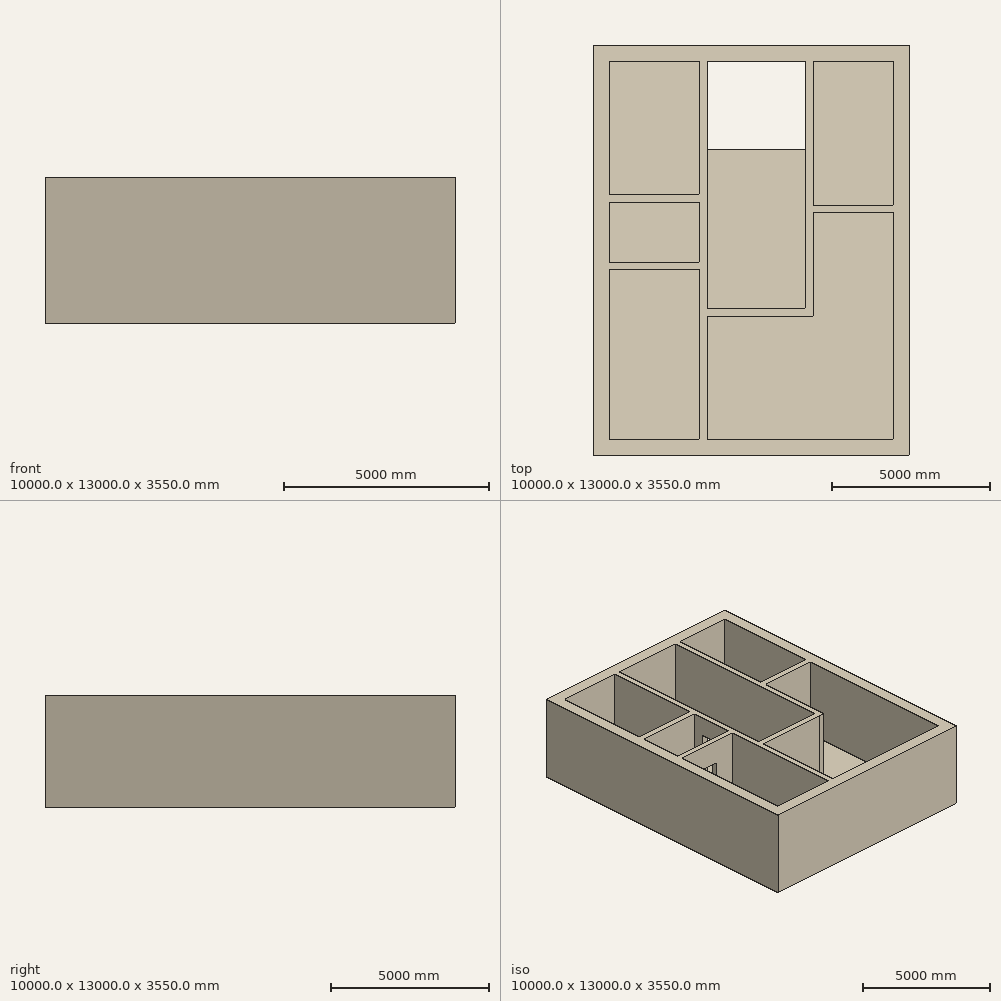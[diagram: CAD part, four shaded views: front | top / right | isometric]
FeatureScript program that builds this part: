
annotation { "Feature Type Name" : "Feature", "Feature Type Description" : "" }
export const myFeature = defineFeature(function(context is Context, id is Id, definition is map)
    precondition{}
    {
        {
            var Q0;
            Q0=qCreatedBy(makeId("Top.planeOp"),FACE);
            var sketch = newSketch(context, id + "F0", { "sketchPlane" : qUnion([Q0])});
            skLineSegment(sketch, "E0.bottom", {"start": v(5000, 6500) * mm, "end": v(-5000, 6500) * mm});
            skLineSegment(sketch, "E0.top", {"start": v(5000, -6500) * mm, "end": v(-5000, -6500) * mm});
            skLineSegment(sketch, "E0.left", {"start": v(5000, 6500) * mm, "end": v(5000, -6500) * mm});
            skLineSegment(sketch, "E0.right", {"start": v(-5000, 6500) * mm, "end": v(-5000, -6500) * mm});
            skPoint(sketch, "E0.middle", {"position": v(0, 0) * mm});
            skSolve(sketch);
        }
        {
            var Q0;
            Q0=qSketchRegion(id+"F0",true);
            extrude(context, id + "F1", {"entities" : qUnion([Q0]), "depth" : 3550 * mm, "offsetDistance" : 25 * mm});
        }
        {
            var Q0;
            Q0=makeQuery(id+"F1.opExtrude","CAP_FACE",FACE,{"disambiguationData":[OSD([sQuery(id+"F0.wireOp",EDGE,"E0.bottom"),sQuery(id+"F0.wireOp",EDGE,"E0.top"),sQuery(id+"F0.wireOp",EDGE,"E0.left"),sQuery(id+"F0.wireOp",EDGE,"E0.right")])],"isStart":false});
            var sketch = newSketch(context, id + "F2", { "sketchPlane" : qUnion([Q0])});
            skLineSegment(sketch, "E1.0", {"start": v(-4500, 6000) * mm, "end": v(-4500, -6000) * mm});
            skLineSegment(sketch, "E1.1", {"start": v(4500, 6000) * mm, "end": v(-4500, 6000) * mm});
            skLineSegment(sketch, "E1.2", {"start": v(4500, 6000) * mm, "end": v(4500, -6000) * mm});
            skLineSegment(sketch, "E1.3", {"start": v(4500, -6000) * mm, "end": v(-4500, -6000) * mm});
            skSolve(sketch);
        }
        {
            var Q0;
            Q0=qSketchRegion(id+"F2",true);
            var Q1;
            Q1=makeQuery(id+"F2.imprint","IMPRINT",FACE,{"disambiguationData":[TD([[makeQuery(id+"F2.imprint","IMPRINT",EDGE,{"derivedFrom":sQuery(id+"F2.wireOp",EDGE,"6241154e-0bf6-49ba-bd71-02362f76f25d.0")}),1.0]])]});
            extrude(context, id + "F3", {"entities" : qUnion([Q0, Q1]), "operationType" : NewBodyOperationType.REMOVE, "oppositeDirection" : true, "depth" : 3300 * mm, "offsetDistance" : 25 * mm});
        }
        {
            var Q0;
            Q0=makeQuery(id+"F3.boolean.opBoolean","COPY",FACE,{"derivedFrom":makeQuery(id+"F3.opExtrude","CAP_FACE",FACE,{"disambiguationData":[OSD([sQuery(id+"F2.wireOp",EDGE,"E1.0"),sQuery(id+"F2.wireOp",EDGE,"E1.1"),sQuery(id+"F2.wireOp",EDGE,"E1.2"),sQuery(id+"F2.wireOp",EDGE,"E1.3")])],"isStart":false})});
            var sketch = newSketch(context, id + "F4", { "sketchPlane" : qUnion([Q0])});
            skLineSegment(sketch, "E2", {"start": v(-4500, -366.62) * mm, "end": v(-1660.5, -366.62) * mm});
            skLineSegment(sketch, "E3", {"start": v(-1660.5, -616.62) * mm, "end": v(-1660.5, -6000) * mm});
            skLineSegment(sketch, "E4", {"start": v(-1660.5, -366.62) * mm, "end": v(-1660.5, 1531.45) * mm});
            skLineSegment(sketch, "E5", {"start": v(-1660.5, 1531.45) * mm, "end": v(-4500, 1531.45) * mm});
            skLineSegment(sketch, "E6", {"start": v(-4500, 1531.45) * mm, "end": v(-1660.5, 1531.45) * mm});
            skLineSegment(sketch, "E7", {"start": v(-1660.5, 1781.45) * mm, "end": v(-1660.5, 6000) * mm});
            skLineSegment(sketch, "E8", {"start": v(1725.2, 1441.9) * mm, "end": v(1725.2, 6000) * mm});
            skLineSegment(sketch, "E9", {"start": v(1975.2, 1441.9) * mm, "end": v(4500, 1441.9) * mm});
            skLineSegment(sketch, "E10", {"start": v(1725.2, 1441.9) * mm, "end": v(1725.2, -1827.54) * mm});
            skLineSegment(sketch, "E11", {"start": v(-1410.5, -2077.54) * mm, "end": v(1725.2, -2077.54) * mm});
            skLineSegment(sketch, "E12.0", {"start": v(-4500, -616.62) * mm, "end": v(-1660.5, -616.62) * mm});
            skLineSegment(sketch, "E13.0", {"start": v(-1410.5, 6000) * mm, "end": v(-1410.5, -1827.54) * mm});
            skLineSegment(sketch, "E14.0", {"start": v(-4500, 1781.45) * mm, "end": v(-1660.5, 1781.45) * mm});
            skLineSegment(sketch, "E15.0", {"start": v(-1410.5, -1827.54) * mm, "end": v(1725.2, -1827.54) * mm});
            skLineSegment(sketch, "E16.trimOffspring", {"start": v(-1410.5, -2077.54) * mm, "end": v(-1410.5, -6000) * mm});
            skLineSegment(sketch, "E17.0", {"start": v(1975.2, 1441.9) * mm, "end": v(1975.2, 6000) * mm});
            skLineSegment(sketch, "E18.0", {"start": v(1975.19, 1191.9) * mm, "end": v(4500, 1191.9) * mm});
            skLineSegment(sketch, "E19.0", {"start": v(1975.19, 1191.9) * mm, "end": v(1975.13, -2083.27) * mm});
            skLineSegment(sketch, "E20", {"start": v(1975.13, -2083.27) * mm, "end": v(1725.2, -2077.54) * mm});
            skLineSegment(sketch, "E21", {"start": v(4500, 1191.9) * mm, "end": v(4500, 1441.9) * mm});
            skLineSegment(sketch, "E22", {"start": v(1975.2, 6000) * mm, "end": v(1725.2, 6000) * mm});
            skLineSegment(sketch, "E23", {"start": v(-1410.5, 6000) * mm, "end": v(-1660.5, 6000) * mm});
            skLineSegment(sketch, "E24", {"start": v(-4500, 1781.45) * mm, "end": v(-4500, 1531.45) * mm});
            skLineSegment(sketch, "E25", {"start": v(-4500, -366.62) * mm, "end": v(-4500, -616.62) * mm});
            skLineSegment(sketch, "E26", {"start": v(-1660.5, -6000) * mm, "end": v(-1410.5, -6000) * mm});
            skSolve(sketch);
        }
        {
            var Q0;
            Q0=makeQuery(id+"F4.imprint","IMPRINT",FACE,{"disambiguationData":[TD([[makeQuery(id+"F4.imprint","IMPRINT",EDGE,{"derivedFrom":sQuery(id+"F4.wireOp",EDGE,"E2")}),-1.0]])]});
            extrude(context, id + "F5", {"entities" : qUnion([Q0]), "operationType" : NewBodyOperationType.ADD, "depth" : 3300 * mm, "offsetDistance" : 25 * mm});
        }
        {
            var Q0;
            Q0=makeQuery(id+"F5.opExtrude","SWEPT_FACE",FACE,{"disambiguationData":[OSD([sQuery(id+"F4.wireOp",EDGE,"E12.0")])]});
            var sketch = newSketch(context, id + "F6", { "sketchPlane" : qUnion([Q0])});
            skLineSegment(sketch, "E27.bottom", {"start": v(-3580.25, 250) * mm, "end": v(-2580.25, 250) * mm});
            skLineSegment(sketch, "E27.top", {"start": v(-3580.25, 2550) * mm, "end": v(-2580.25, 2550) * mm});
            skLineSegment(sketch, "E27.left", {"start": v(-3580.25, 250) * mm, "end": v(-3580.25, 2550) * mm});
            skLineSegment(sketch, "E27.right", {"start": v(-2580.25, 250) * mm, "end": v(-2580.25, 2550) * mm});
            skLineSegment(sketch, "E28", {"start": v(-3580.25, 2550) * mm, "end": v(-4500, 2550) * mm, "construction": true});
            skLineSegment(sketch, "E29", {"start": v(-2580.25, 2550) * mm, "end": v(-1660.5, 2550) * mm, "construction": true});
            skSolve(sketch);
        }
        {
            var Q0;
            Q0=makeQuery(id+"F6.imprint","IMPRINT",FACE,{"disambiguationData":[TD([[makeQuery(id+"F6.imprint","IMPRINT",EDGE,{"derivedFrom":sQuery(id+"F6.wireOp",EDGE,"E27.bottom")}),1.0]])]});
            extrude(context, id + "F7", {"entities" : qUnion([Q0]), "operationType" : NewBodyOperationType.REMOVE, "oppositeDirection" : true, "depth" : 250 * mm, "offsetDistance" : 25 * mm});
        }
        {
            var Q0;
            Q0=makeQuery(id+"F5.opExtrude","SWEPT_FACE",FACE,{"disambiguationData":[OSD([sQuery(id+"F4.wireOp",EDGE,"E4")])]});
            var sketch = newSketch(context, id + "F8", { "sketchPlane" : qUnion([Q0])});
            skLineSegment(sketch, "E30.bottom", {"start": v(-82.41, 250) * mm, "end": v(-1082.41, 250) * mm});
            skLineSegment(sketch, "E30.top", {"start": v(-82.41, 2750) * mm, "end": v(-1082.41, 2750) * mm});
            skLineSegment(sketch, "E30.left", {"start": v(-82.41, 250) * mm, "end": v(-82.41, 2750) * mm});
            skLineSegment(sketch, "E30.right", {"start": v(-1082.41, 250) * mm, "end": v(-1082.41, 2750) * mm});
            skLineSegment(sketch, "E31", {"start": v(-1082.41, 2750) * mm, "end": v(-1531.45, 2750) * mm, "construction": true});
            skLineSegment(sketch, "E32", {"start": v(-82.41, 2750) * mm, "end": v(366.62, 2750) * mm, "construction": true});
            skSolve(sketch);
        }
        {
            var Q0;
            Q0=qSketchRegion(id+"F8",true);
            var Q1;
            Q1=makeQuery(id+"F5.opExtrude","SWEPT_FACE",FACE,{"disambiguationData":[OSD([sQuery(id+"F4.wireOp",EDGE,"E13.0")])]});
            extrude(context, id + "F9", {"entities" : qUnion([Q0]), "operationType" : NewBodyOperationType.REMOVE, "endBound" : BoundingType.UP_TO_SURFACE, "oppositeDirection" : true, "depth" : 25 * mm, "endBoundEntityFace" : qUnion([Q1]), "offsetDistance" : 25 * mm});
        }
        {
            var Q0;
            {var subQ0=sQuery(id+"F2.wireOp",EDGE,"E1.0");var subQ2=sQuery(id+"F2.wireOp",EDGE,"E1.3");var subQ3=sQuery(id+"F2.wireOp",EDGE,"E1.1");var subQ4=makeQuery(id+"F3.boolean.opBoolean","COPY",FACE,{"derivedFrom":makeQuery(id+"F3.opExtrude","CAP_FACE",FACE,{"disambiguationData":[OSD([subQ0,subQ3,sQuery(id+"F2.wireOp",EDGE,"E1.2"),subQ2])],"isStart":false})});Q0=makeQuery(id+"F9.boolean.opBoolean","MERGE",FACE,{"derivedFrom":[makeQuery(id+"F5.boolean.opBoolean","SPLIT",FACE,{"disambiguationData":[TD([makeQuery(id+"F5.opExtrude","SWEPT_FACE",FACE,{"disambiguationData":[OSD([sQuery(id+"F4.wireOp",EDGE,"E13.0")])]})])],"derivedFrom":subQ4}),makeQuery(id+"F7.boolean.opBoolean","MERGE",FACE,{"derivedFrom":[makeQuery(id+"F5.boolean.opBoolean","SPLIT",FACE,{"disambiguationData":[TD([makeQuery(id+"F5.opExtrude","SWEPT_FACE",FACE,{"disambiguationData":[OSD([sQuery(id+"F4.wireOp",EDGE,"E2")])]})])],"derivedFrom":subQ4}),makeQuery(id+"F5.boolean.opBoolean","SPLIT",FACE,{"disambiguationData":[TD([makeQuery(id+"F5.opExtrude","SWEPT_FACE",FACE,{"disambiguationData":[OSD([sQuery(id+"F4.wireOp",EDGE,"E3")])]})])],"derivedFrom":subQ4}),makeQuery(id+"F7.opExtrude","SWEPT_FACE",FACE,{"disambiguationData":[OSD([sQuery(id+"F6.wireOp",EDGE,"E27.bottom")])]})]}),makeQuery(id+"F9.opExtrude","SWEPT_FACE",FACE,{"disambiguationData":[OSD([sQuery(id+"F8.wireOp",EDGE,"E30.bottom")])]})]});}
            var sketch = newSketch(context, id + "F10", { "sketchPlane" : qUnion([Q0])});
            skLineSegment(sketch, "E33.bottom", {"start": v(-1410.5, 3200) * mm, "end": v(1725.2, 3200) * mm});
            skLineSegment(sketch, "E33.top", {"start": v(-1410.5, 6000) * mm, "end": v(1725.2, 6000) * mm});
            skLineSegment(sketch, "E33.left", {"start": v(-1410.5, 3200) * mm, "end": v(-1410.5, 6000) * mm});
            skLineSegment(sketch, "E33.right", {"start": v(1725.2, 3200) * mm, "end": v(1725.2, 6000) * mm});
            skSolve(sketch);
        }
        {
            var Q0;
            Q0=makeQuery(id+"F10.imprint","IMPRINT",FACE,{"disambiguationData":[TD([[makeQuery(id+"F10.imprint","IMPRINT",EDGE,{"derivedFrom":sQuery(id+"F10.wireOp",EDGE,"E33.bottom")}),1.0]])]});
            extrude(context, id + "F11", {"entities" : qUnion([Q0]), "operationType" : NewBodyOperationType.REMOVE, "endBound" : BoundingType.UP_TO_NEXT, "oppositeDirection" : true, "depth" : 25 * mm, "offsetDistance" : 25 * mm});
        }
    });
